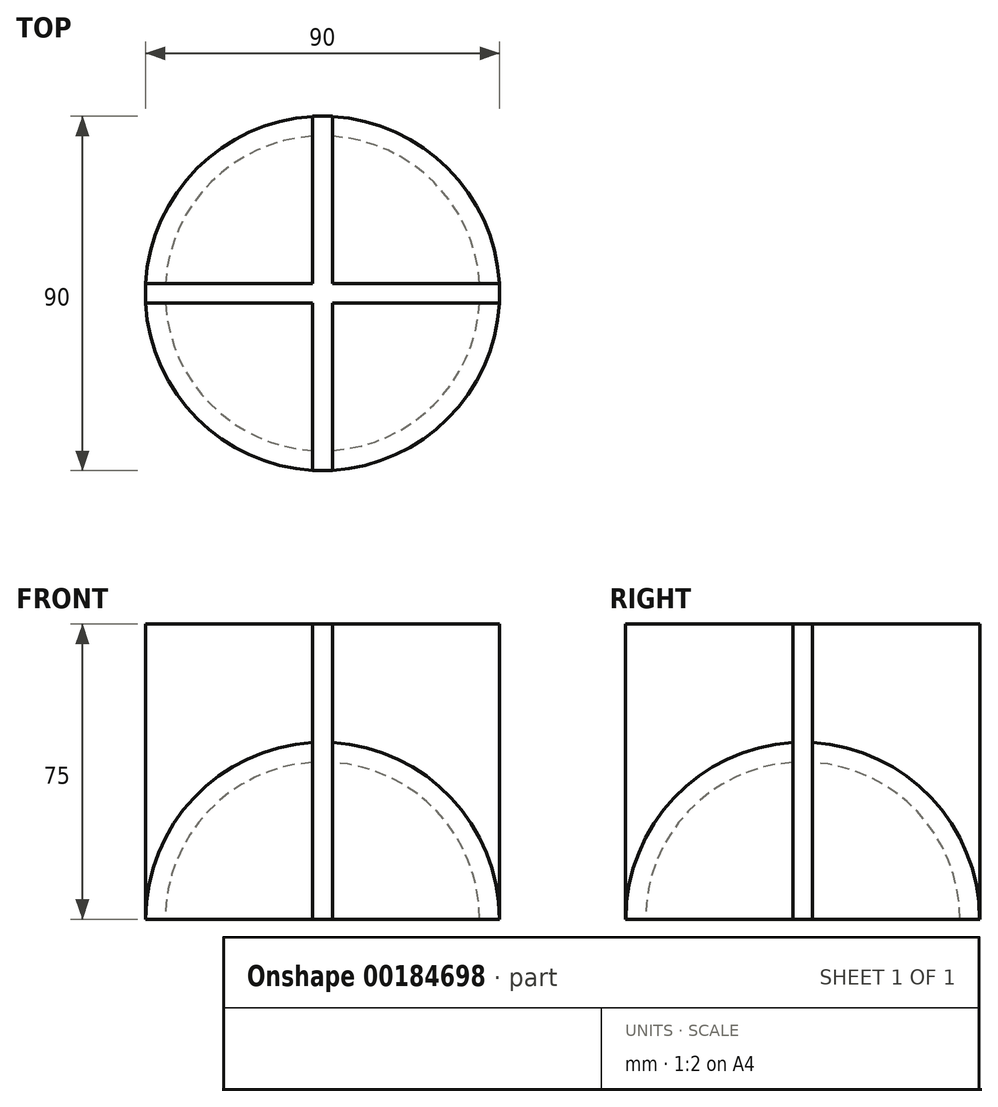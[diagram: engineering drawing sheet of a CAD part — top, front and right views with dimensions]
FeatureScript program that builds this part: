
annotation { "Feature Type Name" : "Feature", "Feature Type Description" : "" }
export const myFeature = defineFeature(function(context is Context, id is Id, definition is map)
    precondition{}
    {
        {
            var Q0;
            Q0=qCreatedBy(makeId("Front.planeOp"),FACE);
            var sketch = newSketch(context, id + "F0", { "sketchPlane" : qUnion([Q0])});
            skArc(sketch, "E0", {"start": v(0, 40) * mm, "mid": v(28.28, 28.28) * mm, "end": v(40, 0) * mm});
            skArc(sketch, "E1", {"start": v(0, 45) * mm, "mid": v(31.82, 31.82) * mm, "end": v(45, 0) * mm});
            skLineSegment(sketch, "E2", {"start": v(0, 40) * mm, "end": v(0, 45) * mm});
            skLineSegment(sketch, "E3", {"start": v(40, 0) * mm, "end": v(45, 0) * mm});
            skSolve(sketch);
        }
        {
            var Q0;
            Q0 = qSketchRegion(id + "F0", true);
            var Q1;
            Q1=sQuery(id+"F0.wireOp",EDGE,"E2");
            revolve(context, id + "F1", {"entities" : qUnion([Q0]), "axis" : qUnion([Q1]), "revolveType" : RevolveType.FULL});
        }
        {
            var Q0;
            Q0=qCreatedBy(makeId("Top.planeOp"),FACE);
            var sketch = newSketch(context, id + "F2", { "sketchPlane" : qUnion([Q0])});
            skLineSegment(sketch, "E4.bottom", {"start": v(45, -2.5) * mm, "end": v(2.5, -2.5) * mm});
            skLineSegment(sketch, "E4.top", {"start": v(45, 2.5) * mm, "end": v(2.5, 2.5) * mm});
            skLineSegment(sketch, "E4.left", {"start": v(45, -2.5) * mm, "end": v(45, 2.5) * mm});
            skLineSegment(sketch, "E4.right", {"start": v(-45, -2.5) * mm, "end": v(-45, 2.5) * mm});
            skPoint(sketch, "E4.middle", {"position": v(0, 0) * mm});
            skLineSegment(sketch, "E5.bottom", {"start": v(-2.5, -45) * mm, "end": v(2.5, -45) * mm});
            skLineSegment(sketch, "E5.top", {"start": v(-2.5, 45) * mm, "end": v(2.5, 45) * mm});
            skLineSegment(sketch, "E5.left", {"start": v(-2.5, -45) * mm, "end": v(-2.5, -2.5) * mm});
            skLineSegment(sketch, "E5.right", {"start": v(2.5, -45) * mm, "end": v(2.5, -2.5) * mm});
            skLineSegment(sketch, "E6.trimOffspring", {"start": v(-2.5, 2.5) * mm, "end": v(-2.5, 45) * mm});
            skLineSegment(sketch, "E7.trimOffspring", {"start": v(-2.5, 2.5) * mm, "end": v(-45, 2.5) * mm});
            skLineSegment(sketch, "E8.trimOffspring", {"start": v(2.5, 2.5) * mm, "end": v(2.5, 45) * mm});
            skLineSegment(sketch, "E9.trimOffspring", {"start": v(-2.5, -2.5) * mm, "end": v(-45, -2.5) * mm});
            skSolve(sketch);
        }
        {
            var Q0;
            Q0 = qSketchRegion(id + "F2", true);
            extrude(context, id + "F3", {"entities" : qUnion([Q0]), "operationType" : NewBodyOperationType.ADD, "depth" : 75 * mm});
        }
    });
